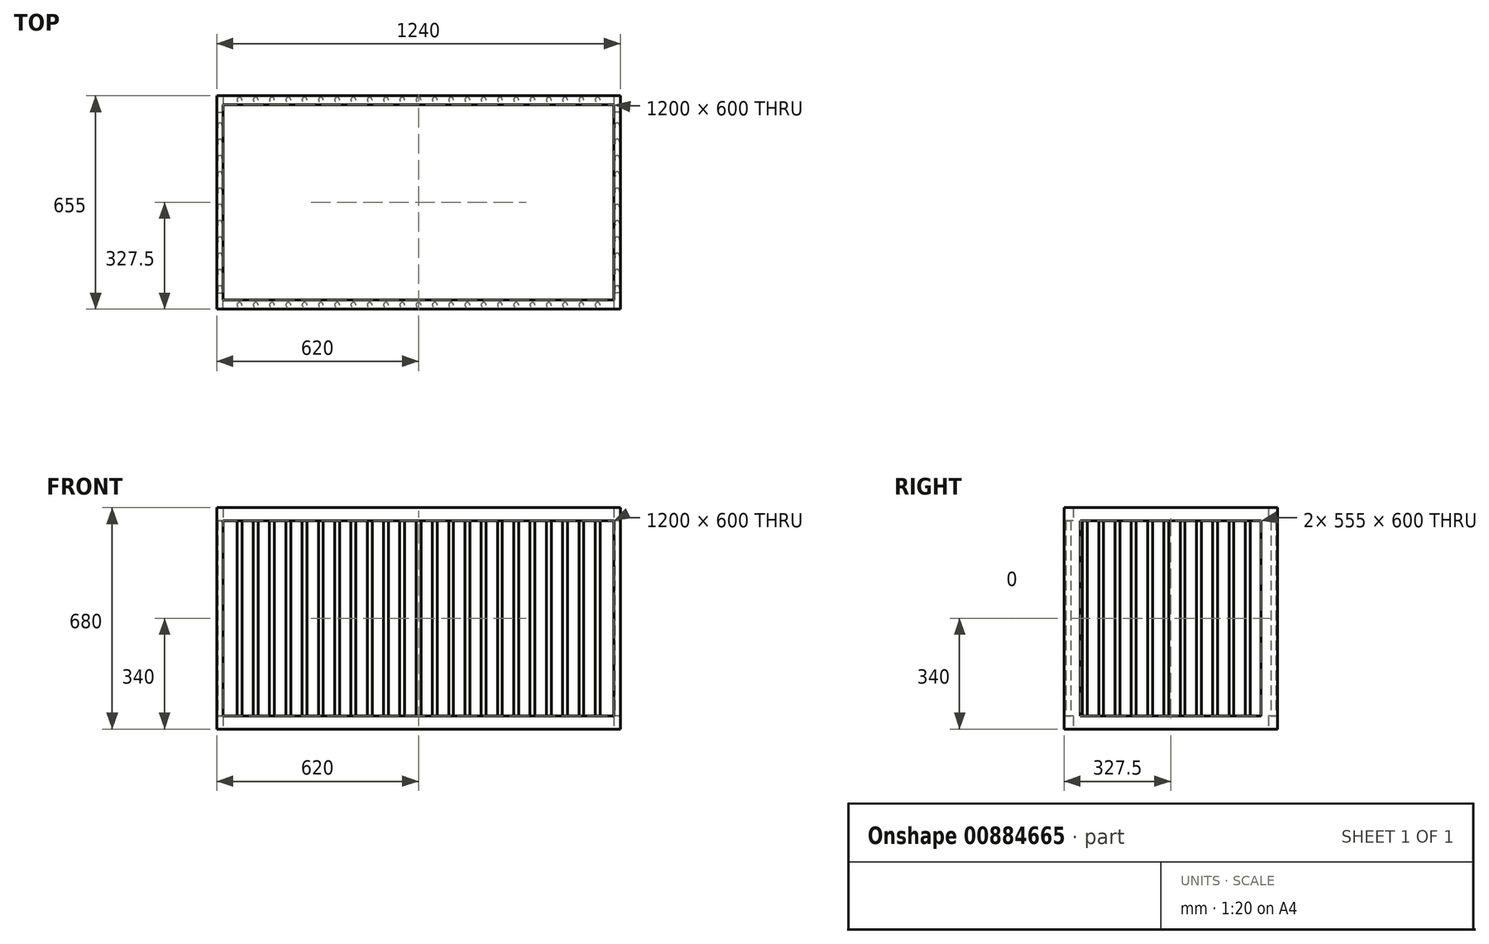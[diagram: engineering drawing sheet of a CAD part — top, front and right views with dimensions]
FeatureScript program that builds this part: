
annotation { "Feature Type Name" : "Feature", "Feature Type Description" : "" }
export const myFeature = defineFeature(function(context is Context, id is Id, definition is map)
    precondition{}
    {
        {
            var Q0;
            Q0=qCreatedBy(makeId("Top.planeOp"),FACE);
            var sketch = newSketch(context, id + "F0", { "sketchPlane" : qUnion([Q0])});
            skLineSegment(sketch, "E0.bottom", {"start": v(620, 327.5) * mm, "end": v(-620, 327.5) * mm});
            skLineSegment(sketch, "E0.top", {"start": v(620, -327.5) * mm, "end": v(-620, -327.5) * mm});
            skLineSegment(sketch, "E0.left", {"start": v(620, 327.5) * mm, "end": v(620, -327.5) * mm});
            skLineSegment(sketch, "E0.right", {"start": v(-620, 327.5) * mm, "end": v(-620, -327.5) * mm});
            skPoint(sketch, "E0.middle", {"position": v(0, 0) * mm});
            skLineSegment(sketch, "E1.bottom", {"start": v(600, 300) * mm, "end": v(-600, 300) * mm});
            skLineSegment(sketch, "E1.top", {"start": v(600, -300) * mm, "end": v(-600, -300) * mm});
            skLineSegment(sketch, "E1.left", {"start": v(600, 300) * mm, "end": v(600, -300) * mm});
            skLineSegment(sketch, "E1.right", {"start": v(-600, 300) * mm, "end": v(-600, -300) * mm});
            skSolve(sketch);
        }
        {
            var Q0;
            Q0=makeQuery(id+"F0.imprint","IMPRINT",FACE,{"disambiguationData":[TD([[makeQuery(id+"F0.imprint","IMPRINT",EDGE,{"derivedFrom":sQuery(id+"F0.wireOp",EDGE,"E0.bottom")}),1.0]])]});
            extrude(context, id + "F1", {"entities" : qUnion([Q0]), "depth" : 40 * mm, "offsetDistance" : 25 * mm});
        }
        {
            var Q0;
            Q0=makeQuery(id+"F1.opExtrude","CAP_FACE",FACE,{"disambiguationData":[OSD([sQuery(id+"F0.wireOp",EDGE,"E0.bottom"),sQuery(id+"F0.wireOp",EDGE,"E0.top"),sQuery(id+"F0.wireOp",EDGE,"E0.left"),sQuery(id+"F0.wireOp",EDGE,"E0.right"),sQuery(id+"F0.wireOp",EDGE,"E1.bottom"),sQuery(id+"F0.wireOp",EDGE,"E1.top"),sQuery(id+"F0.wireOp",EDGE,"E1.left"),sQuery(id+"F0.wireOp",EDGE,"E1.right")])],"isStart":false});
            var sketch = newSketch(context, id + "F2", { "sketchPlane" : qUnion([Q0])});
            skLineSegment(sketch, "E2.bottom", {"start": v(-620, 327.5) * mm, "end": v(-600, 327.5) * mm});
            skLineSegment(sketch, "E2.top", {"start": v(-620, 277.5) * mm, "end": v(-600, 277.5) * mm});
            skLineSegment(sketch, "E2.left", {"start": v(-620, 327.5) * mm, "end": v(-620, 277.5) * mm});
            skLineSegment(sketch, "E2.right", {"start": v(-600, 327.5) * mm, "end": v(-600, 277.5) * mm});
            skLineSegment(sketch, "E3", {"start": v(-660.99, 0) * mm, "end": v(668.53, 0) * mm, "construction": true});
            skLineSegment(sketch, "E4", {"start": v(0, 362.65) * mm, "end": v(0, -358.88) * mm, "construction": true});
            skPoint(sketch, "E4.startSnap0", {"position": v(0, 327.5) * mm});
            skLineSegment(sketch, "E5.MirrorCS", {"start": v(620, 327.5) * mm, "end": v(600, 327.5) * mm});
            skLineSegment(sketch, "E6.MirrorCS", {"start": v(600, 327.5) * mm, "end": v(600, 277.5) * mm});
            skLineSegment(sketch, "E7.MirrorCS", {"start": v(620, 327.5) * mm, "end": v(620, 277.5) * mm});
            skLineSegment(sketch, "E8.MirrorCS", {"start": v(620, 277.5) * mm, "end": v(600, 277.5) * mm});
            skLineSegment(sketch, "E9.MirrorCS", {"start": v(-620, -277.5) * mm, "end": v(-600, -277.5) * mm});
            skLineSegment(sketch, "E10.MirrorCS", {"start": v(620, -327.5) * mm, "end": v(600, -327.5) * mm});
            skLineSegment(sketch, "E11.MirrorCS", {"start": v(620, -277.5) * mm, "end": v(600, -277.5) * mm});
            skLineSegment(sketch, "E12.MirrorCS", {"start": v(-620, -327.5) * mm, "end": v(-600, -327.5) * mm});
            skLineSegment(sketch, "E13.MirrorCS", {"start": v(-620, -327.5) * mm, "end": v(-620, -277.5) * mm});
            skLineSegment(sketch, "E14.MirrorCS", {"start": v(620, -327.5) * mm, "end": v(620, -277.5) * mm});
            skPoint(sketch, "E15.MirrorP", {"position": v(0, -327.5) * mm});
            skLineSegment(sketch, "E16.MirrorCS", {"start": v(-600, -327.5) * mm, "end": v(-600, -277.5) * mm});
            skLineSegment(sketch, "E17.MirrorCS", {"start": v(600, -327.5) * mm, "end": v(600, -277.5) * mm});
            skSolve(sketch);
        }
        {
            var Q0;
            {var subQ2=sQuery(id+"F2.wireOp",EDGE,"E2.top");Q0=makeQuery(id+"F2.imprint","IMPRINT",FACE,{"disambiguationData":[TD([[makeQuery(id+"F2.imprint","IMPRINT",EDGE,{"derivedFrom":subQ2}),1.0]])]});}
            var Q1;
            {var subQ2=sQuery(id+"F2.wireOp",EDGE,"E12.MirrorCS");Q1=makeQuery(id+"F2.imprint","IMPRINT",FACE,{"disambiguationData":[TD([[makeQuery(id+"F2.imprint","IMPRINT",EDGE,{"derivedFrom":subQ2}),-1.0]])]});}
            var Q2;
            {var subQ3=sQuery(id+"F2.wireOp",EDGE,"E5.MirrorCS");Q2=makeQuery(id+"F2.imprint","IMPRINT",FACE,{"disambiguationData":[TD([[makeQuery(id+"F2.imprint","IMPRINT",EDGE,{"derivedFrom":subQ3}),1.0]])]});}
            var Q3;
            {var subQ3=sQuery(id+"F2.wireOp",EDGE,"E10.MirrorCS");Q3=makeQuery(id+"F2.imprint","IMPRINT",FACE,{"disambiguationData":[TD([[makeQuery(id+"F2.imprint","IMPRINT",EDGE,{"derivedFrom":subQ3}),-1.0]])]});}
            extrude(context, id + "F3", {"entities" : qUnion([Q0, Q1, Q2, Q3]), "operationType" : NewBodyOperationType.ADD, "depth" : 600 * mm, "offsetDistance" : 25 * mm});
        }
        {
            var Q0;
            {var subQ0=sQuery(id+"F0.wireOp",EDGE,"E1.right");var subQ1=sQuery(id+"F0.wireOp",EDGE,"E1.top");var subQ2=sQuery(id+"F0.wireOp",EDGE,"E1.left");var subQ3=sQuery(id+"F0.wireOp",EDGE,"E0.top");Q0=makeQuery(id+"F3.boolean.opBoolean","SPLIT",FACE,{"disambiguationData":[TD([makeQuery(id+"F1.opExtrude","SWEPT_FACE",FACE,{"disambiguationData":[OSD([subQ3])]})])],"derivedFrom":makeQuery(id+"F1.opExtrude","CAP_FACE",FACE,{"disambiguationData":[OSD([sQuery(id+"F0.wireOp",EDGE,"E0.bottom"),subQ3,sQuery(id+"F0.wireOp",EDGE,"E0.left"),sQuery(id+"F0.wireOp",EDGE,"E0.right"),sQuery(id+"F0.wireOp",EDGE,"E1.bottom"),subQ1,subQ2,subQ0])],"isStart":false})});}
            var sketch = newSketch(context, id + "F4", { "sketchPlane" : qUnion([Q0])});
            skCircle(sketch, "E18", {"center": v(-550, -315) * mm, "radius": 7.5 * mm});
            skCircle(sketch, "E19.1.0.0", {"center": v(-500, -315) * mm, "radius": 7.5 * mm});
            skCircle(sketch, "E19.2.0.0", {"center": v(-450, -315) * mm, "radius": 7.5 * mm});
            skCircle(sketch, "E19.3.0.0", {"center": v(-400, -315) * mm, "radius": 7.5 * mm});
            skCircle(sketch, "E19.4.0.0", {"center": v(-350, -315) * mm, "radius": 7.5 * mm});
            skCircle(sketch, "E19.5.0.0", {"center": v(-300, -315) * mm, "radius": 7.5 * mm});
            skCircle(sketch, "E19.6.0.0", {"center": v(-250, -315) * mm, "radius": 7.5 * mm});
            skCircle(sketch, "E19.7.0.0", {"center": v(-200, -315) * mm, "radius": 7.5 * mm});
            skCircle(sketch, "E19.8.0.0", {"center": v(-150, -315) * mm, "radius": 7.5 * mm});
            skCircle(sketch, "E19.9.0.0", {"center": v(-100, -315) * mm, "radius": 7.5 * mm});
            skLineSegment(sketch, "E19.direction1", {"start": v(-550, -315) * mm, "end": v(-500, -315) * mm, "construction": true});
            skCircle(sketch, "E20.0.10.0", {"center": v(-50, -315) * mm, "radius": 7.5 * mm});
            skCircle(sketch, "E20.0.11.0", {"center": v(0, -315) * mm, "radius": 7.5 * mm});
            skCircle(sketch, "E20.0.12.0", {"center": v(50, -315) * mm, "radius": 7.5 * mm});
            skCircle(sketch, "E20.0.13.0", {"center": v(100, -315) * mm, "radius": 7.5 * mm});
            skCircle(sketch, "E20.0.14.0", {"center": v(150, -315) * mm, "radius": 7.5 * mm});
            skCircle(sketch, "E20.0.15.0", {"center": v(200, -315) * mm, "radius": 7.5 * mm});
            skCircle(sketch, "E20.0.16.0", {"center": v(250, -315) * mm, "radius": 7.5 * mm});
            skCircle(sketch, "E20.0.17.0", {"center": v(300, -315) * mm, "radius": 7.5 * mm});
            skCircle(sketch, "E20.0.18.0", {"center": v(350, -315) * mm, "radius": 7.5 * mm});
            skCircle(sketch, "E20.0.19.0", {"center": v(400, -315) * mm, "radius": 7.5 * mm});
            skCircle(sketch, "E21.0.20.0", {"center": v(450, -315) * mm, "radius": 7.5 * mm});
            skCircle(sketch, "E21.0.21.0", {"center": v(500, -315) * mm, "radius": 7.5 * mm});
            skCircle(sketch, "E21.0.22.0", {"center": v(550, -315) * mm, "radius": 7.5 * mm});
            skLineSegment(sketch, "E22", {"start": v(-680.4, 0) * mm, "end": v(780.85, 0) * mm, "construction": true});
            skLineSegment(sketch, "E23", {"start": v(0, 353.86) * mm, "end": v(0, -371.66) * mm, "construction": true});
            skCircle(sketch, "E24.MirrorC", {"center": v(-500, 315) * mm, "radius": 7.5 * mm});
            skCircle(sketch, "E25.MirrorC", {"center": v(-550, 315) * mm, "radius": 7.5 * mm});
            skCircle(sketch, "E26.MirrorC", {"center": v(150, 315) * mm, "radius": 7.5 * mm});
            skCircle(sketch, "E27.MirrorC", {"center": v(0, 315) * mm, "radius": 7.5 * mm});
            skCircle(sketch, "E28.MirrorC", {"center": v(250, 315) * mm, "radius": 7.5 * mm});
            skCircle(sketch, "E29.MirrorC", {"center": v(-400, 315) * mm, "radius": 7.5 * mm});
            skCircle(sketch, "E30.MirrorC", {"center": v(450, 315) * mm, "radius": 7.5 * mm});
            skCircle(sketch, "E31.MirrorC", {"center": v(100, 315) * mm, "radius": 7.5 * mm});
            skCircle(sketch, "E32.MirrorC", {"center": v(500, 315) * mm, "radius": 7.5 * mm});
            skCircle(sketch, "E33.MirrorC", {"center": v(-100, 315) * mm, "radius": 7.5 * mm});
            skCircle(sketch, "E34.MirrorC", {"center": v(-450, 315) * mm, "radius": 7.5 * mm});
            skCircle(sketch, "E35.MirrorC", {"center": v(400, 315) * mm, "radius": 7.5 * mm});
            skCircle(sketch, "E36.MirrorC", {"center": v(50, 315) * mm, "radius": 7.5 * mm});
            skCircle(sketch, "E37.MirrorC", {"center": v(-300, 315) * mm, "radius": 7.5 * mm});
            skCircle(sketch, "E38.MirrorC", {"center": v(-50, 315) * mm, "radius": 7.5 * mm});
            skCircle(sketch, "E39.MirrorC", {"center": v(550, 315) * mm, "radius": 7.5 * mm});
            skCircle(sketch, "E40.MirrorC", {"center": v(300, 315) * mm, "radius": 7.5 * mm});
            skCircle(sketch, "E41.MirrorC", {"center": v(-200, 315) * mm, "radius": 7.5 * mm});
            skCircle(sketch, "E42.MirrorC", {"center": v(200, 315) * mm, "radius": 7.5 * mm});
            skCircle(sketch, "E43.MirrorC", {"center": v(350, 315) * mm, "radius": 7.5 * mm});
            skCircle(sketch, "E44.MirrorC", {"center": v(-250, 315) * mm, "radius": 7.5 * mm});
            skCircle(sketch, "E45.MirrorC", {"center": v(-150, 315) * mm, "radius": 7.5 * mm});
            skCircle(sketch, "E46.MirrorC", {"center": v(-350, 315) * mm, "radius": 7.5 * mm});
            skLineSegment(sketch, "E47.MirrorCS", {"start": v(-550, 315) * mm, "end": v(-500, 315) * mm, "construction": true});
            skCircle(sketch, "E48", {"center": v(-610, -263.75) * mm, "radius": 7.5 * mm});
            skCircle(sketch, "E49.0.1.0", {"center": v(-610, -213.75) * mm, "radius": 7.5 * mm});
            skCircle(sketch, "E49.0.2.0", {"center": v(-610, -163.75) * mm, "radius": 7.5 * mm});
            skCircle(sketch, "E49.0.3.0", {"center": v(-610, -113.75) * mm, "radius": 7.5 * mm});
            skCircle(sketch, "E49.0.4.0", {"center": v(-610, -63.75) * mm, "radius": 7.5 * mm});
            skCircle(sketch, "E49.0.5.0", {"center": v(-610, -13.75) * mm, "radius": 7.5 * mm});
            skCircle(sketch, "E49.0.6.0", {"center": v(-610, 36.25) * mm, "radius": 7.5 * mm});
            skCircle(sketch, "E49.0.7.0", {"center": v(-610, 86.25) * mm, "radius": 7.5 * mm});
            skCircle(sketch, "E49.0.8.0", {"center": v(-610, 136.25) * mm, "radius": 7.5 * mm});
            skCircle(sketch, "E49.0.9.0", {"center": v(-610, 186.25) * mm, "radius": 7.5 * mm});
            skCircle(sketch, "E49.0.10.0", {"center": v(-610, 236.25) * mm, "radius": 7.5 * mm});
            skLineSegment(sketch, "E49.direction1", {"start": v(-610, -263.75) * mm, "end": v(-585, -263.75) * mm, "construction": true});
            skLineSegment(sketch, "E49.direction2", {"start": v(-610, -263.75) * mm, "end": v(-610, -213.75) * mm, "construction": true});
            skCircle(sketch, "E50.MirrorC", {"center": v(610, -263.75) * mm, "radius": 7.5 * mm});
            skCircle(sketch, "E51.MirrorC", {"center": v(610, -213.75) * mm, "radius": 7.5 * mm});
            skCircle(sketch, "E52.MirrorC", {"center": v(610, 136.25) * mm, "radius": 7.5 * mm});
            skCircle(sketch, "E53.MirrorC", {"center": v(610, 236.25) * mm, "radius": 7.5 * mm});
            skCircle(sketch, "E54.MirrorC", {"center": v(610, -113.75) * mm, "radius": 7.5 * mm});
            skCircle(sketch, "E55.MirrorC", {"center": v(610, 86.25) * mm, "radius": 7.5 * mm});
            skCircle(sketch, "E56.MirrorC", {"center": v(610, 186.25) * mm, "radius": 7.5 * mm});
            skCircle(sketch, "E57.MirrorC", {"center": v(610, 36.25) * mm, "radius": 7.5 * mm});
            skCircle(sketch, "E58.MirrorC", {"center": v(610, -13.75) * mm, "radius": 7.5 * mm});
            skCircle(sketch, "E59.MirrorC", {"center": v(610, -63.75) * mm, "radius": 7.5 * mm});
            skCircle(sketch, "E60.MirrorC", {"center": v(610, -163.75) * mm, "radius": 7.5 * mm});
            skLineSegment(sketch, "E61.MirrorCS", {"start": v(610, -263.75) * mm, "end": v(585, -263.75) * mm, "construction": true});
            skLineSegment(sketch, "E62.MirrorCS", {"start": v(610, -263.75) * mm, "end": v(610, -213.75) * mm, "construction": true});
            skSolve(sketch);
        }
        {
            var Q0;
            Q0 = qSketchRegion(id + "F4", true);
            extrude(context, id + "F5", {"entities" : qUnion([Q0]), "operationType" : NewBodyOperationType.ADD, "depth" : 600 * mm, "offsetDistance" : 25 * mm});
        }
        {
            var Q0;
            Q0=makeQuery(id+"F3.opExtrude","CAP_FACE",FACE,{"disambiguationData":[OSD([sQuery(id+"F2.wireOp",EDGE,"E2.top"),sQuery(id+"F2.wireOp",EDGE,"E2.bottom"),sQuery(id+"F2.wireOp",EDGE,"E2.left"),sQuery(id+"F2.wireOp",EDGE,"E2.right")])],"isStart":false});
            var sketch = newSketch(context, id + "F6", { "sketchPlane" : qUnion([Q0])});
            skLineSegment(sketch, "E63.0.0", {"start": v(620, -327.5) * mm, "end": v(-620, -327.5) * mm});
            skLineSegment(sketch, "E63.0.1", {"start": v(-620, -327.5) * mm, "end": v(-620, 327.5) * mm});
            skLineSegment(sketch, "E63.0.2", {"start": v(-620, 327.5) * mm, "end": v(620, 327.5) * mm});
            skLineSegment(sketch, "E63.0.3", {"start": v(620, 327.5) * mm, "end": v(620, -327.5) * mm});
            skLineSegment(sketch, "E64.0", {"start": v(600, -300) * mm, "end": v(-600, -300) * mm});
            skLineSegment(sketch, "E65.0", {"start": v(-600, 300) * mm, "end": v(-600, -300) * mm});
            skLineSegment(sketch, "E66.0", {"start": v(600, 300) * mm, "end": v(-600, 300) * mm});
            skLineSegment(sketch, "E67.0", {"start": v(600, 300) * mm, "end": v(600, -300) * mm});
            skSolve(sketch);
        }
        {
            var Q0;
            Q0 = qSketchRegion(id + "F6", true);
            extrude(context, id + "F7", {"entities" : qUnion([Q0]), "operationType" : NewBodyOperationType.ADD, "depth" : 40 * mm, "offsetDistance" : 25 * mm});
        }
    });
